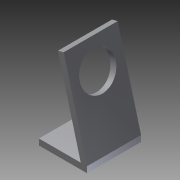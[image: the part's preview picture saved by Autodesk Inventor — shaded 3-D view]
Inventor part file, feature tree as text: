
AUTODESK INVENTOR PART (.ipt)
format: ipt  version: 2012 (Build 160160000, 160)  size: 90,112 bytes
history: native  units: in
note: dims shown in document units (in); Inventor stores cm internally (conversion verified against a paired STEP export)
features: extrude x2, sketch x2
ambient origin geometry x8: Origin, YZ Plane, XZ Plane, XY Plane, X Axis, Y Axis, Z Axis, Center Point
bodies: Solid1 (feature_tree)
feature tree (4):
  extrude  "Extrusion1"  Depth=1.0in
  extrude  "Extrusion2"  TaperAngle=75.0deg  [1 undecoded]
  sketch  "Sketch1"  dims[d0=0.125in d1=1.0in]
  sketch  "Sketch2"  dims[d3=0.125in d4=75.0deg d5=1.875in d6=1.125in d7=0.0in d8=0.75in d9=0.5625in d10=0.5625in d11=1.125in d12=0.0in]
note: 1 required parameter value undecoded (feature->parameter linkage not recoverable at this tier; creation-order binding heuristic only, values carry confidence <= 0.55)
